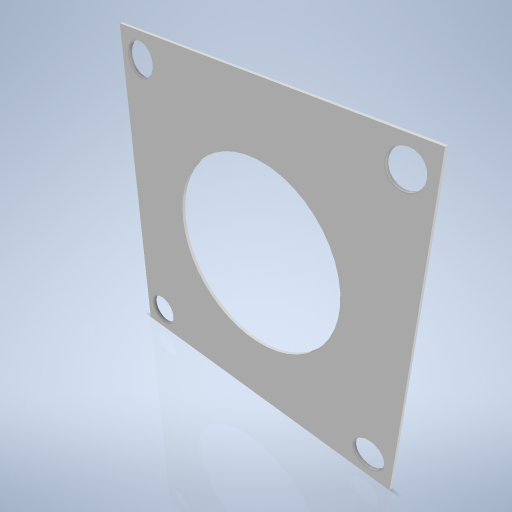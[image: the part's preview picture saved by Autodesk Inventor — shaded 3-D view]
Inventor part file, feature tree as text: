
AUTODESK INVENTOR PART (.ipt)
format: ipt  version: 2024.2 (Build 282272000, 272)  size: 251,392 bytes
history: native  units: mm
features: sketch x3, other x2, hole x2
ambient origin geometry x8: Origin, YZ Plane, XZ Plane, XY Plane, X Axis, Y Axis, Z Axis, Center Point
bodies: Volumenkörper1 (feature_tree)
feature tree (7):
  other  "Fläche1"
  hole  "Bohrung1"  [1 undecoded]
  hole  "Bohrung2"  [1 undecoded]
  sketch  "Skizze1"  dims[d0=50.0mm d1=50.0mm]
  other  "Grobblech1"
  sketch  "Skizze2"  dims[d2=0.5mm]
  sketch  "Skizze3"  dims[d3=29.0mm d4=6.0mm d5=4.0mm d6=2.0mm d7=90.0deg d8=0.5mm d9=20.594885mm d10=5.0mm d11=6.0mm d12=4.0mm d13=2.0mm d14=90.0deg d15=8.0mm d16=20.594885mm d17=42.248mm d19=42.248mm]
note: 2 required parameter values undecoded (feature->parameter linkage not recoverable at this tier; creation-order binding heuristic only, values carry confidence <= 0.55)
